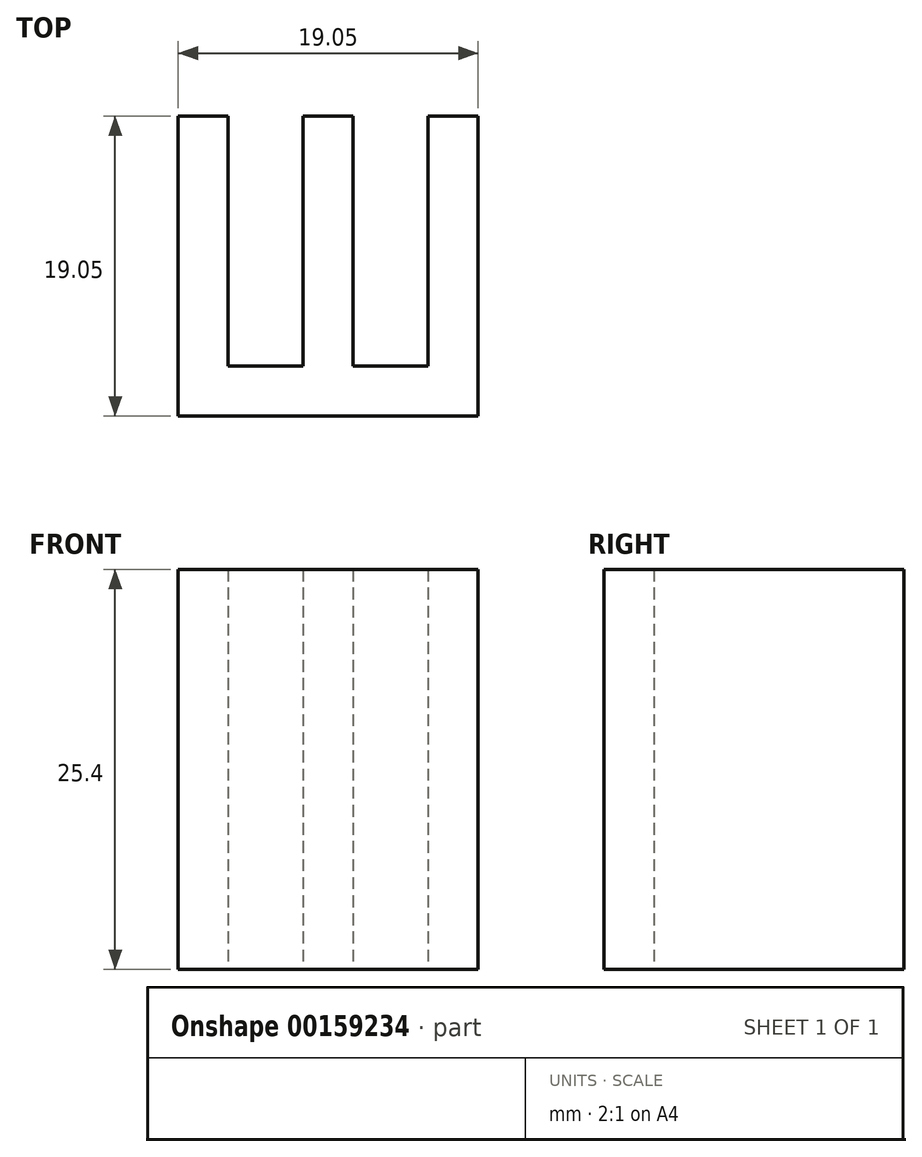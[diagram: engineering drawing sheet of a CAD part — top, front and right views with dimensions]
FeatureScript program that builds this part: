
annotation { "Feature Type Name" : "Feature", "Feature Type Description" : "" }
export const myFeature = defineFeature(function(context is Context, id is Id, definition is map)
    precondition{}
    {
        {
            var Q0;
            Q0=qCreatedBy(makeId("Top.planeOp"),FACE);
            var sketch = newSketch(context, id + "F0", { "sketchPlane" : qUnion([Q0])});
            skLineSegment(sketch, "E0", {"start": v(0, 0) * mm, "end": v(0, 19.05) * mm});
            skLineSegment(sketch, "E1", {"start": v(0, 19.05) * mm, "end": v(3.18, 19.05) * mm});
            skLineSegment(sketch, "E2", {"start": v(3.17, 19.05) * mm, "end": v(3.17, 3.18) * mm});
            skLineSegment(sketch, "E3", {"start": v(3.17, 3.18) * mm, "end": v(7.94, 3.18) * mm});
            skLineSegment(sketch, "E4", {"start": v(7.94, 3.18) * mm, "end": v(7.94, 19.05) * mm});
            skLineSegment(sketch, "E5", {"start": v(7.94, 19.05) * mm, "end": v(11.11, 19.05) * mm});
            skLineSegment(sketch, "E6", {"start": v(11.11, 19.05) * mm, "end": v(11.11, 3.18) * mm});
            skLineSegment(sketch, "E7", {"start": v(11.11, 3.18) * mm, "end": v(15.88, 3.18) * mm});
            skLineSegment(sketch, "E8", {"start": v(15.88, 3.18) * mm, "end": v(15.88, 19.05) * mm});
            skLineSegment(sketch, "E9", {"start": v(15.88, 19.05) * mm, "end": v(19.05, 19.05) * mm});
            skLineSegment(sketch, "E10", {"start": v(19.05, 19.05) * mm, "end": v(19.05, 0) * mm});
            skLineSegment(sketch, "E11", {"start": v(19.05, 0) * mm, "end": v(0, 0) * mm});
            skLineSegment(sketch, "E12", {"start": v(5.56, 3.18) * mm, "end": v(5.56, 0) * mm, "construction": true});
            skLineSegment(sketch, "E13", {"start": v(13.5, 3.18) * mm, "end": v(13.5, 0) * mm, "construction": true});
            skLineSegment(sketch, "E14", {"start": v(0, 19.05) * mm, "end": v(26.16, 19.05) * mm, "construction": true});
            skSolve(sketch);
        }
        {
            var Q0;
            Q0 = qSketchRegion(id + "F0", true);
            extrude(context, id + "F1", {"entities" : qUnion([Q0]), "depth" : 25.4 * mm});
        }
    });
